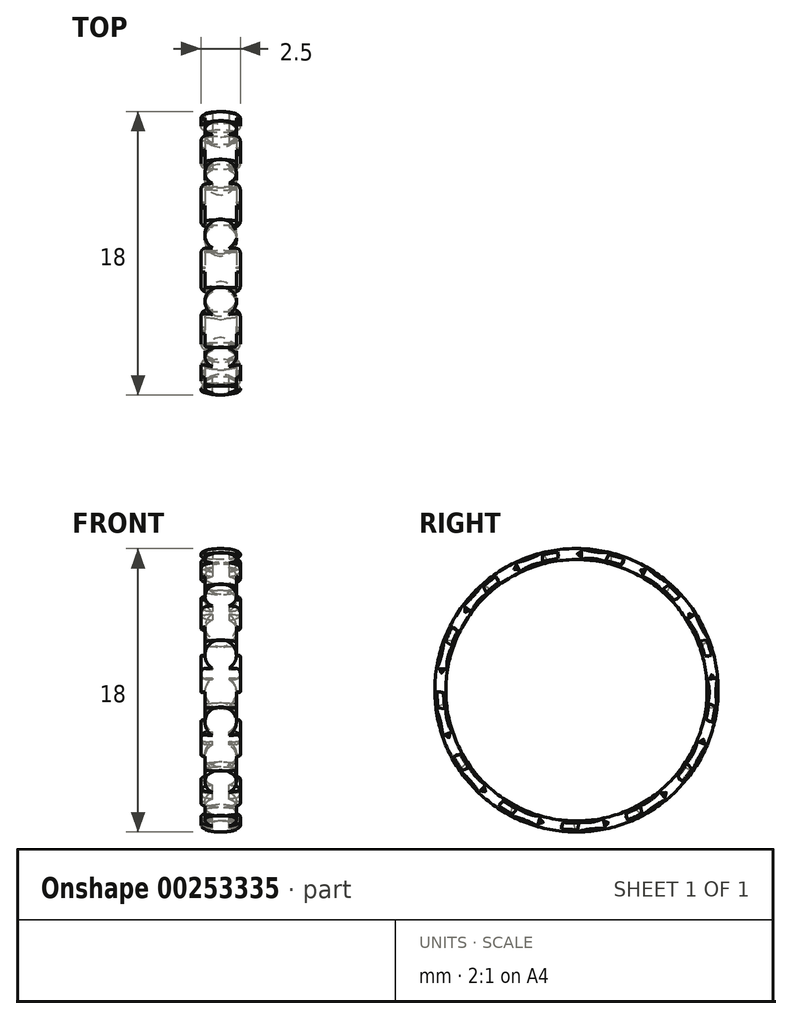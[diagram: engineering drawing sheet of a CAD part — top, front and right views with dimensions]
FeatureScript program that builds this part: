
annotation { "Feature Type Name" : "Feature", "Feature Type Description" : "" }
export const myFeature = defineFeature(function(context is Context, id is Id, definition is map)
    precondition{}
    {
        {
            var Q0;
            Q0=qCreatedBy(makeId("Top.planeOp"),FACE);
            var sketch = newSketch(context, id + "F0", { "sketchPlane" : qUnion([Q0])});
            skLineSegment(sketch, "E0.top", {"start": v(-0.95, -2.17) * mm, "end": v(0.95, -2.17) * mm});
            skLineSegment(sketch, "E0.left", {"start": v(-1, -1.17) * mm, "end": v(-1, -2.12) * mm});
            skLineSegment(sketch, "E0.right", {"start": v(1, -1.17) * mm, "end": v(1, -2.12) * mm});
            skLineSegment(sketch, "E1.bottom", {"start": v(-1.2, -1.18) * mm, "end": v(-1, -1.18) * mm});
            skLineSegment(sketch, "E1.top", {"start": v(-0.95, 0.32) * mm, "end": v(-0.53, 0.32) * mm});
            skLineSegment(sketch, "E1.left", {"start": v(-1.25, -1.12) * mm, "end": v(-1.25, 0.02) * mm});
            skLineSegment(sketch, "E1.right", {"start": v(1.25, -1.13) * mm, "end": v(1.25, 0.02) * mm});
            skPoint(sketch, "E2.centerSnap0", {"position": v(0, 0.32) * mm});
            skLineSegment(sketch, "E3.trimOffspring", {"start": v(1, -1.18) * mm, "end": v(1.2, -1.18) * mm});
            skLineSegment(sketch, "E4.trimOffspring", {"start": v(0.53, 0.32) * mm, "end": v(0.95, 0.32) * mm});
            skArc(sketch, "E5", {"start": v(0.53, 0.33) * mm, "mid": v(0, 2.17) * mm, "end": v(-0.53, 0.33) * mm});
            skPoint(sketch, "E6.visualSharp", {"position": v(1.25, 0.33) * mm});
            skArc(sketch, "E6.filletArc", {"start": v(1.25, 0.02) * mm, "mid": v(1.16, 0.24) * mm, "end": v(0.95, 0.32) * mm});
            skPoint(sketch, "E7.visualSharp", {"position": v(-1.25, 0.32) * mm});
            skArc(sketch, "E7.filletArc", {"start": v(-0.95, 0.33) * mm, "mid": v(-1.16, 0.24) * mm, "end": v(-1.25, 0.02) * mm});
            skPoint(sketch, "E8.visualSharp", {"position": v(-1.25, -1.18) * mm});
            skArc(sketch, "E8.filletArc", {"start": v(-1.25, -1.13) * mm, "mid": v(-1.24, -1.16) * mm, "end": v(-1.2, -1.18) * mm});
            skPoint(sketch, "E9.visualSharp", {"position": v(1.25, -1.18) * mm});
            skArc(sketch, "E9.filletArc", {"start": v(1.2, -1.18) * mm, "mid": v(1.24, -1.16) * mm, "end": v(1.25, -1.13) * mm});
            skPoint(sketch, "E10.visualSharp", {"position": v(-1, -2.18) * mm});
            skArc(sketch, "E10.filletArc", {"start": v(-1, -2.13) * mm, "mid": v(-0.99, -2.16) * mm, "end": v(-0.95, -2.17) * mm});
            skPoint(sketch, "E11.visualSharp", {"position": v(1, -2.17) * mm});
            skArc(sketch, "E11.filletArc", {"start": v(0.95, -2.17) * mm, "mid": v(0.99, -2.16) * mm, "end": v(1, -2.12) * mm});
            skLineSegment(sketch, "E12", {"start": v(0, -2.17) * mm, "end": v(0, 2.17) * mm});
            skLineSegment(sketch, "E13", {"start": v(0, 2.17) * mm, "end": v(0, 0) * mm});
            skLineSegment(sketch, "E14", {"start": v(0, 0) * mm, "end": v(1.25, 0) * mm});
            skLineSegment(sketch, "E15", {"start": v(1.25, 0) * mm, "end": v(0, 0) * mm});
            skLineSegment(sketch, "E16", {"start": v(-1.25, 0) * mm, "end": v(0, 0) * mm});
            skSolve(sketch);
        }
        {
            var Q0;
            Q0=makeQuery(id+"F0.imprint","IMPRINT",FACE,{"disambiguationData":[TD([[makeQuery(id+"F0.imprint","IMPRINT",EDGE,{"derivedFrom":sQuery(id+"F0.wireOp",EDGE,"E0.top")}),1.0]])]});
            var Q1;
            {var subQ2=sQuery(id+"F0.wireOp",EDGE,"E1.top");Q1=makeQuery(id+"F0.imprint","IMPRINT",FACE,{"disambiguationData":[TD([[makeQuery(id+"F0.imprint","IMPRINT",EDGE,{"derivedFrom":subQ2}),-1.0]])]});}
            var Q2;
            {var subQ2=sQuery(id+"F0.wireOp",EDGE,"E4.trimOffspring");Q2=makeQuery(id+"F0.imprint","IMPRINT",FACE,{"disambiguationData":[TD([[makeQuery(id+"F0.imprint","IMPRINT",EDGE,{"derivedFrom":subQ2}),-1.0]])]});}
            extrude(context, id + "F1", {"entities" : qUnion([Q0, Q1, Q2]), "depth" : 10 * mm});
        }
        {
            var Q0;
            Q0=qCreatedBy(makeId("Right.planeOp"),FACE);
            var sketch = newSketch(context, id + "F2", { "sketchPlane" : qUnion([Q0])});
            skCircle(sketch, "E17", {"center": v(0, 0) * mm, "radius": 8.3 * mm});
            skCircle(sketch, "E18", {"center": v(0, 0) * mm, "radius": 9 * mm});
            skSolve(sketch);
        }
        {
            var Q0;
            Q0=makeQuery(id+"F2.imprint","IMPRINT",FACE,{"disambiguationData":[TD([[makeQuery(id+"F2.imprint","IMPRINT",EDGE,{"derivedFrom":sQuery(id+"F2.wireOp",EDGE,"E17")}),-1.0]])]});
            extrude(context, id + "F3", {"entities" : qUnion([Q0]), "operationType" : NewBodyOperationType.INTERSECT, "depth" : 5 * mm, "symmetric" : true});
        }
        {
            var Q0;
            Q0=qCreatedBy(makeId("Front.planeOp"),FACE);
            var sketch = newSketch(context, id + "F4", { "sketchPlane" : qUnion([Q0])});
            skEllipse(sketch, "E19", {"center": v(0, 8.65) * mm, "majorRadius": 0.35 * mm, "minorRadius": 1.25 * mm, "majorAxis": v(0, -1)});
            skSolve(sketch);
        }
        {
            var Q0;
            Q0=qCreatedBy(makeId("Right.planeOp"),FACE);
            var sketch = newSketch(context, id + "F5", { "sketchPlane" : qUnion([Q0])});
            skCircle(sketch, "E20", {"center": v(0, 0) * mm, "radius": 8.3 * mm});
            skSolve(sketch);
        }
        {
            var Q0;
            Q0=makeQuery(id+"F4.imprint","IMPRINT",FACE,{"disambiguationData":[TD([[makeQuery(id+"F4.imprint","IMPRINT",EDGE,{"derivedFrom":sQuery(id+"F4.wireOp",EDGE,"E19")}),1.0]])]});
            var Q1;
            Q1=sQuery(id+"F5.wireOp",EDGE,"E20");
            revolve(context, id + "F6", {"operationType" : NewBodyOperationType.INTERSECT, "entities" : qUnion([Q0]), "axis" : qUnion([Q1]), "revolveType" : RevolveType.FULL});
        }
        {
            var Q0;
            Q0=qCreatedBy(makeId("Top.planeOp"),FACE);
            var sketch = newSketch(context, id + "F7", { "sketchPlane" : qUnion([Q0])});
            skLineSegment(sketch, "E21", {"start": v(-5.64, 0) * mm, "end": v(5.83, 0) * mm});
            skSolve(sketch);
        }
        {
            var Q0;
            Q0=makeQuery(id+"F1.opExtrude","SWEPT_BODY",BODY,{"disambiguationData":[OSD([sQuery(id+"F0.wireOp",EDGE,"E0.top"),sQuery(id+"F0.wireOp",EDGE,"E0.left"),sQuery(id+"F0.wireOp",EDGE,"E0.right"),sQuery(id+"F0.wireOp",EDGE,"E1.bottom"),sQuery(id+"F0.wireOp",EDGE,"E1.top"),sQuery(id+"F0.wireOp",EDGE,"E1.left"),sQuery(id+"F0.wireOp",EDGE,"E1.right"),sQuery(id+"F0.wireOp",EDGE,"E3.trimOffspring"),sQuery(id+"F0.wireOp",EDGE,"E4.trimOffspring"),sQuery(id+"F0.wireOp",EDGE,"E5"),sQuery(id+"F0.wireOp",EDGE,"E6.filletArc"),sQuery(id+"F0.wireOp",EDGE,"E7.filletArc"),sQuery(id+"F0.wireOp",EDGE,"E8.filletArc"),sQuery(id+"F0.wireOp",EDGE,"E9.filletArc"),sQuery(id+"F0.wireOp",EDGE,"E10.filletArc"),sQuery(id+"F0.wireOp",EDGE,"E11.filletArc")])]});
            var Q1;
            Q1=sQuery(id+"F7.wireOp",EDGE,"E21");
            circularPattern(context, id + "F8", {"entities" : qUnion([Q0]), "axis" : qUnion([Q1]), "angle" : 360 * degree, "instanceCount" : 13, "equalSpace" : true});
        }
    });
